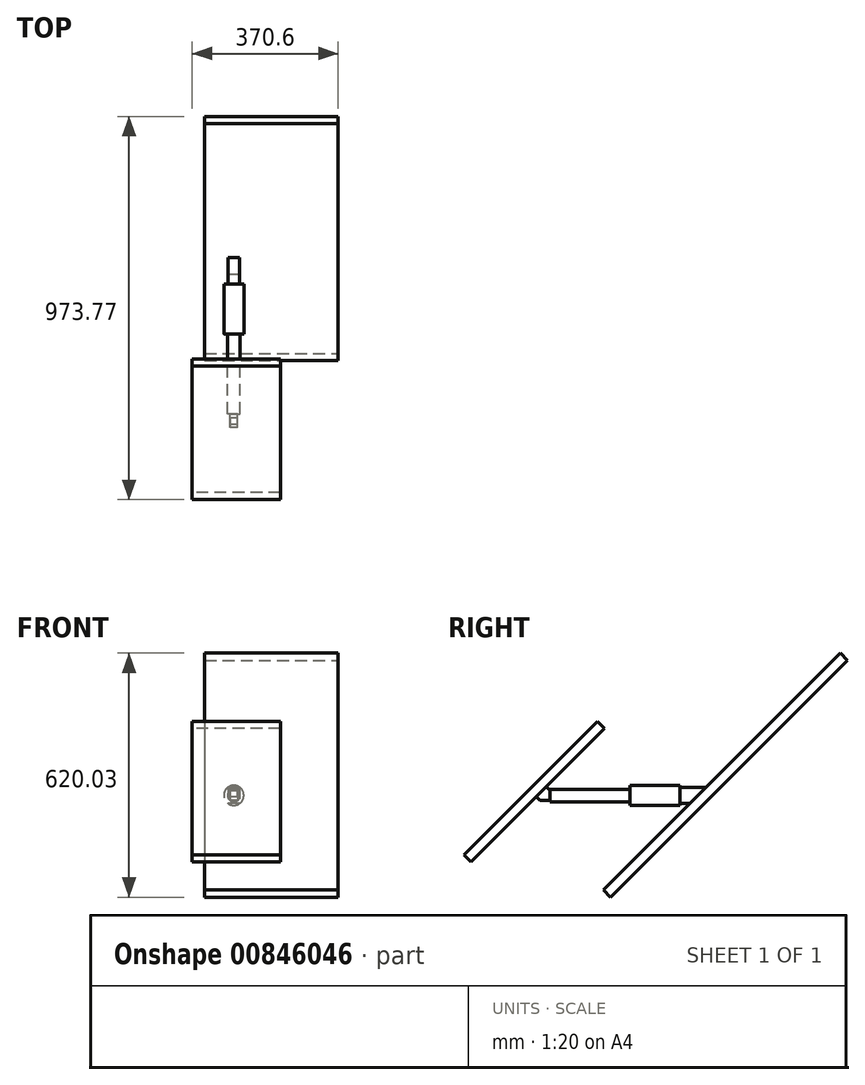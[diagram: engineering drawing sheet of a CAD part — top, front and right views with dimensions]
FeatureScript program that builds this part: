
annotation { "Feature Type Name" : "Feature", "Feature Type Description" : "" }
export const myFeature = defineFeature(function(context is Context, id is Id, definition is map)
    precondition{}
    {
        {
            var Q0;
            Q0=qCreatedBy(makeId("Front.planeOp"),FACE);
            var sketch = newSketch(context, id + "F0", { "sketchPlane" : qUnion([Q0])});
            skCircle(sketch, "E0", {"center": v(0, 0) * mm, "radius": 25.4 * mm});
            skSolve(sketch);
        }
        {
            var Q0;
            Q0 = qSketchRegion(id + "F0", true);
            extrude(context, id + "F1", {"entities" : qUnion([Q0]), "depth" : 127 * mm, "offsetDistance" : 25.4 * mm});
        }
        {
            var Q0;
            Q0=makeQuery(id+"F1.opExtrude","CAP_FACE",FACE,{"disambiguationData":[OSD([sQuery(id+"F0.wireOp",EDGE,"E0")])],"isStart":false});
            var sketch = newSketch(context, id + "F2", { "sketchPlane" : qUnion([Q0])});
            skCircle(sketch, "E1", {"center": v(0, 0) * mm, "radius": 15.88 * mm});
            skSolve(sketch);
        }
        {
            var Q0;
            Q0 = qSketchRegion(id + "F2", true);
            extrude(context, id + "F3", {"entities" : qUnion([Q0]), "operationType" : NewBodyOperationType.ADD, "depth" : 203.2 * mm, "offsetDistance" : 25.4 * mm});
        }
        {
            var Q0;
            Q0=makeQuery(id+"F3.opExtrude","CAP_FACE",FACE,{"disambiguationData":[OSD([sQuery(id+"F2.wireOp",EDGE,"E1")])],"isStart":false});
            var sketch = newSketch(context, id + "F4", { "sketchPlane" : qUnion([Q0])});
            skLineSegment(sketch, "E2.bottom", {"start": v(-9.27, 12.89) * mm, "end": v(9.27, 12.89) * mm});
            skLineSegment(sketch, "E2.top", {"start": v(-9.27, -12.89) * mm, "end": v(9.27, -12.89) * mm});
            skLineSegment(sketch, "E2.left", {"start": v(-9.27, 12.89) * mm, "end": v(-9.27, -12.89) * mm});
            skLineSegment(sketch, "E2.right", {"start": v(9.27, 12.89) * mm, "end": v(9.27, -12.89) * mm});
            skSolve(sketch);
        }
        {
            var Q0;
            Q0 = qSketchRegion(id + "F4", true);
            extrude(context, id + "F5", {"entities" : qUnion([Q0]), "operationType" : NewBodyOperationType.ADD, "depth" : 25.4 * mm, "offsetDistance" : 25.4 * mm});
        }
        {
            var Q0;
            Q0=makeQuery(id+"F5.opExtrude","CAP_EDGE",EDGE,{"disambiguationData":[OSD([sQuery(id+"F4.wireOp",EDGE,"E2.bottom")])],"isStart":false});
            chamfer(context, id + "F6", {"entities" : qUnion([Q0]), "width" : 25.4 * mm, "tangentPropagation" : true});
        }
        {
            var Q0;
            Q0=makeQuery(id+"F6.opChamfer","BLEND_FACE",FACE,{"disambiguationData":[OSD([sQuery(id+"F4.wireOp",EDGE,"E2.bottom")])]});
            var sketch = newSketch(context, id + "F7", { "sketchPlane" : qUnion([Q0])});
            skLineSegment(sketch, "E3.bottom", {"start": v(-9.27, -260.3) * mm, "end": v(9.27, -260.3) * mm});
            skLineSegment(sketch, "E3.top", {"start": v(-9.27, -224.37) * mm, "end": v(9.27, -224.37) * mm});
            skLineSegment(sketch, "E3.left", {"start": v(-9.27, -260.3) * mm, "end": v(-9.27, -224.37) * mm});
            skLineSegment(sketch, "E3.right", {"start": v(9.27, -260.3) * mm, "end": v(9.27, -224.37) * mm});
            skSolve(sketch);
        }
        {
            var Q0;
            Q0 = qSketchRegion(id + "F7", true);
            extrude(context, id + "F8", {"entities" : qUnion([Q0]), "operationType" : NewBodyOperationType.ADD, "depth" : 12.7 * mm, "offsetDistance" : 25.4 * mm});
        }
        {
            var Q0;
            Q0=makeQuery(id+"F1.opExtrude","CAP_FACE",FACE,{"disambiguationData":[OSD([sQuery(id+"F0.wireOp",EDGE,"E0")])],"isStart":true});
            var sketch = newSketch(context, id + "F9", { "sketchPlane" : qUnion([Q0])});
            skLineSegment(sketch, "E4.bottom", {"start": v(-14.81, 20.64) * mm, "end": v(14.81, 20.64) * mm});
            skLineSegment(sketch, "E4.top", {"start": v(-14.81, -20.64) * mm, "end": v(14.81, -20.64) * mm});
            skLineSegment(sketch, "E4.left", {"start": v(-14.81, 20.64) * mm, "end": v(-14.81, -20.64) * mm});
            skLineSegment(sketch, "E4.right", {"start": v(14.81, 20.64) * mm, "end": v(14.81, -20.64) * mm});
            skSolve(sketch);
        }
        {
            var Q0;
            Q0 = qSketchRegion(id + "F9", true);
            extrude(context, id + "F10", {"entities" : qUnion([Q0]), "operationType" : NewBodyOperationType.ADD, "depth" : 76.2 * mm, "offsetDistance" : 25.4 * mm});
        }
        {
            var Q0;
            Q0=makeQuery(id+"F10.opExtrude","CAP_EDGE",EDGE,{"disambiguationData":[OSD([sQuery(id+"F9.wireOp",EDGE,"E4.top")])],"isStart":false});
            chamfer(context, id + "F11", {"entities" : qUnion([Q0]), "width" : 50.8 * mm, "tangentPropagation" : true});
        }
        {
            var Q0;
            Q0=makeQuery(id+"F8.opExtrude","CAP_FACE",FACE,{"disambiguationData":[OSD([sQuery(id+"F7.wireOp",EDGE,"E3.bottom"),sQuery(id+"F7.wireOp",EDGE,"E3.top"),sQuery(id+"F7.wireOp",EDGE,"E3.left"),sQuery(id+"F7.wireOp",EDGE,"E3.right")])],"isStart":false});
            var sketch = newSketch(context, id + "F12", { "sketchPlane" : qUnion([Q0])});
            skLineSegment(sketch, "E5.bottom", {"start": v(118.77, -494.7) * mm, "end": v(-105.92, -494.7) * mm});
            skLineSegment(sketch, "E5.top", {"start": v(118.77, -15.36) * mm, "end": v(-105.92, -15.36) * mm});
            skLineSegment(sketch, "E5.left", {"start": v(118.77, -494.7) * mm, "end": v(118.77, -15.36) * mm});
            skLineSegment(sketch, "E5.right", {"start": v(-105.92, -494.7) * mm, "end": v(-105.92, -15.36) * mm});
            skSolve(sketch);
        }
        {
            var Q0;
            Q0 = qSketchRegion(id + "F12", true);
            extrude(context, id + "F13", {"entities" : qUnion([Q0]), "operationType" : NewBodyOperationType.ADD, "depth" : 25.4 * mm, "offsetDistance" : 25.4 * mm});
        }
        {
            var Q0;
            Q0=makeQuery(id+"F11.opChamfer","BLEND_FACE",FACE,{"disambiguationData":[OSD([sQuery(id+"F9.wireOp",EDGE,"E4.top")])]});
            var sketch = newSketch(context, id + "F14", { "sketchPlane" : qUnion([Q0])});
            skLineSegment(sketch, "E6.bottom", {"start": v(74.31, 543.78) * mm, "end": v(-264.68, 543.78) * mm});
            skLineSegment(sketch, "E6.top", {"start": v(74.31, -307.66) * mm, "end": v(-264.68, -307.66) * mm});
            skLineSegment(sketch, "E6.left", {"start": v(74.31, 543.78) * mm, "end": v(74.31, -307.66) * mm});
            skLineSegment(sketch, "E6.right", {"start": v(-264.68, 543.78) * mm, "end": v(-264.68, -307.66) * mm});
            skSolve(sketch);
        }
        {
            var Q0;
            Q0 = qSketchRegion(id + "F14", true);
            extrude(context, id + "F15", {"entities" : qUnion([Q0]), "operationType" : NewBodyOperationType.ADD, "depth" : 25.4 * mm, "offsetDistance" : 25.4 * mm});
        }
    });
